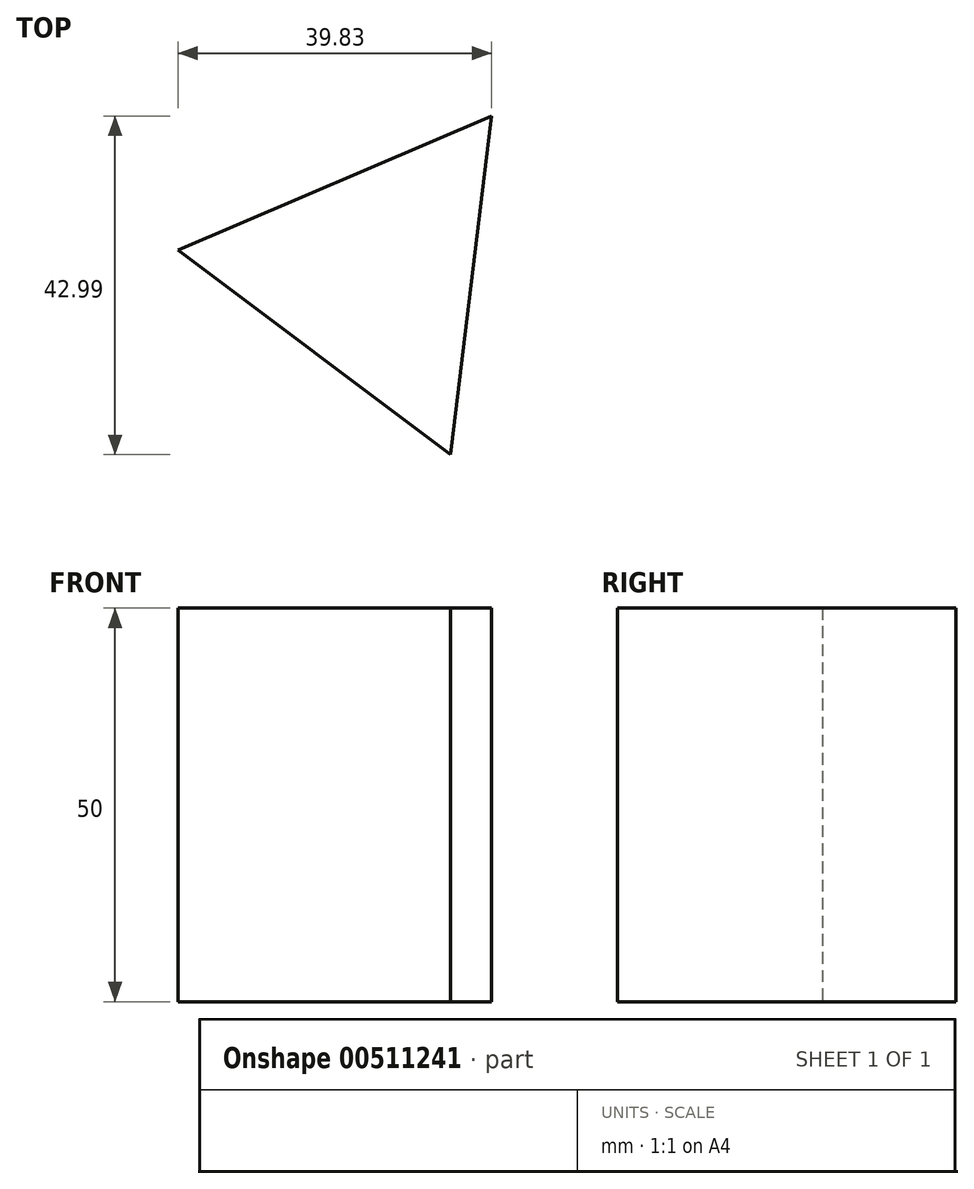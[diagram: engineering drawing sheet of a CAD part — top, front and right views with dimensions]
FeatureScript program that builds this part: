
annotation { "Feature Type Name" : "Feature", "Feature Type Description" : "" }
export const myFeature = defineFeature(function(context is Context, id is Id, definition is map)
    precondition{}
    {
        {
            var Q0;
            Q0=qCreatedBy(makeId("Top.planeOp"),FACE);
            var sketch = newSketch(context, id + "F0", { "sketchPlane" : qUnion([Q0])});
            skCircle(sketch, "E0.cCircle", {"center": v(0, 0) * mm, "radius": 25 * mm, "construction": true});
            skLineSegment(sketch, "E0.0", {"start": v(15.01, 20) * mm, "end": v(9.8, -23) * mm});
            skLineSegment(sketch, "E0.1", {"start": v(9.8, -23) * mm, "end": v(-24.82, 3) * mm});
            skLineSegment(sketch, "E0.2", {"start": v(-24.82, 3) * mm, "end": v(15.01, 20) * mm});
            skSolve(sketch);
        }
        {
            var Q0;
            Q0=makeQuery(id+"F0.imprint","IMPRINT",FACE,{"disambiguationData":[TD([[makeQuery(id+"F0.imprint","IMPRINT",EDGE,{"derivedFrom":sQuery(id+"F0.wireOp",EDGE,"E0.0")}),-1.0]])]});
            extrude(context, id + "F1", {"entities" : qUnion([Q0]), "depth" : 50 * mm});
        }
    });
